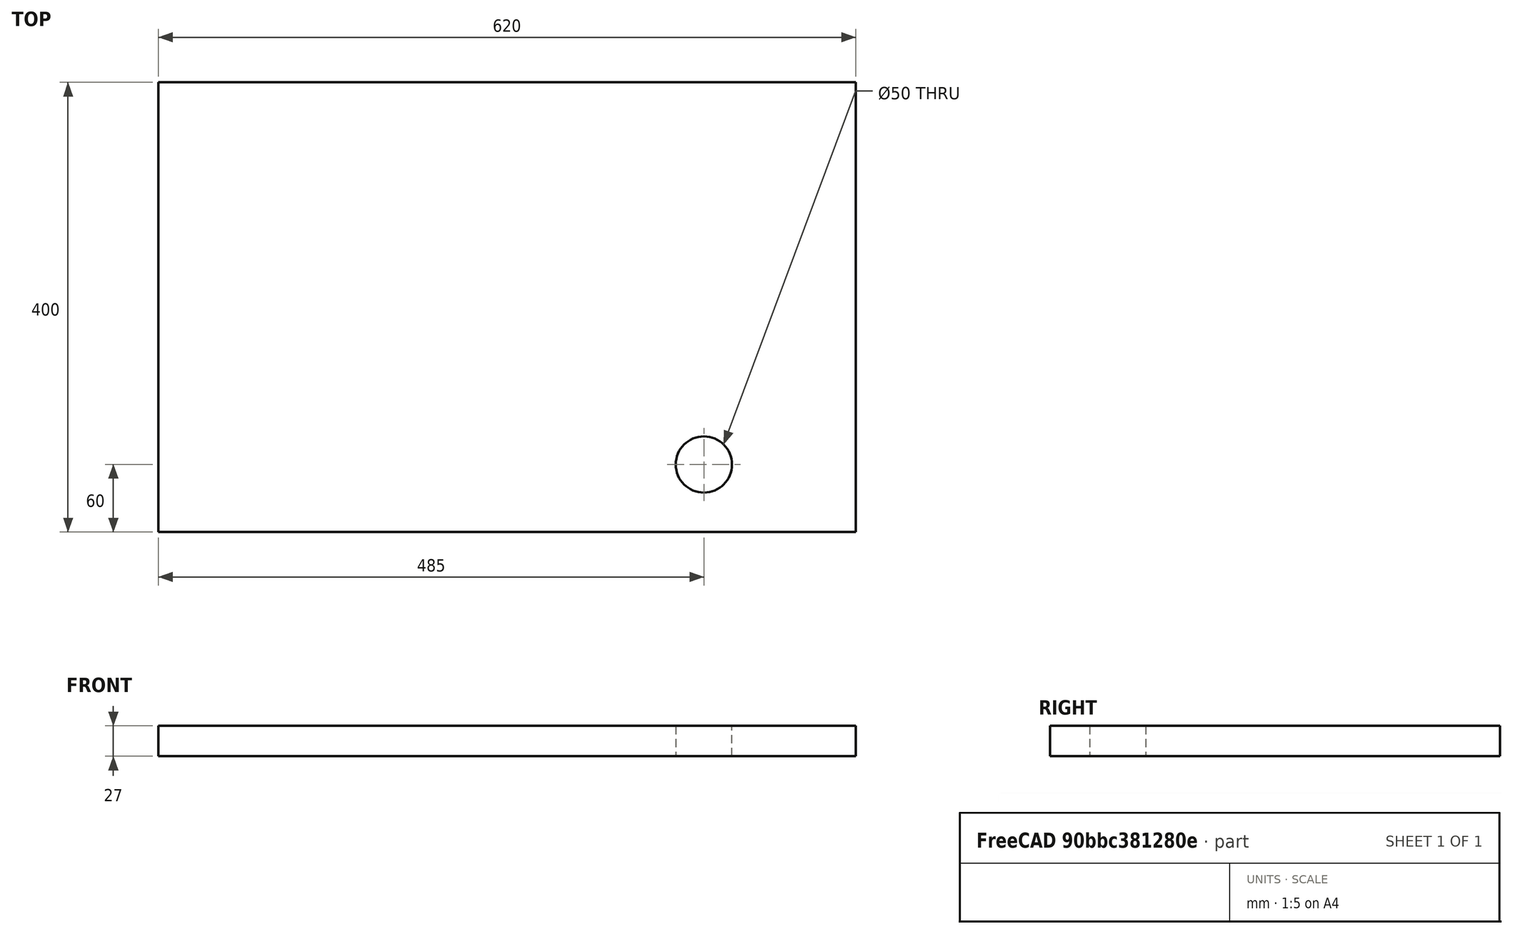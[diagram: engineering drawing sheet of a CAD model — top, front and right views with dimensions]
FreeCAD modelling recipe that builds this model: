
FCSTD DOCUMENT  (FreeCAD 0.20R25131 (Git))
Label: Arbeitsfläche
License: All rights reserved
LicenseURL: http://en.wikipedia.org/wiki/All_rights_reserved
objects: Part::FeaturePython×8, App::FeaturePython×2, Part::Box×1, Part::Cylinder×1, Part::Cut×1
note: 10 computed .brp shape members not serialized (recipe doc carries the construction recipe); baked Part::Feature solids carry a one-line shape summary decoded from their .brp
EXTERNAL_REF file=Grunddaten.FCStd obj=Spreadsheet

FEATURE [Part::Box] Box  label="Cube"
  AttacherType = Attacher::AttachEngine3D
  Height = 27
  Length = 620
  Width = 400
  expr: Length = <<Grunddaten>>#Spreadsheet.Arbeitsflaeche + 2 * <<Grunddaten>>#Spreadsheet.Ueberstand
  expr: Width = <<Grunddaten>>#Spreadsheet.Plattenbreite
  expr: Height = <<Grunddaten>>#Spreadsheet.Plattendicke
FEATURE [App::FeaturePython] Constraints  # WARN: FeaturePython — macro-defined, semantics opaque (R4)
  _Version = 1
FEATURE [Part::Cylinder] Cylinder  label="Schraubzwinge_oben"
  Angle = 360
  AttacherType = Attacher::AttachEngine3D
  FirstAngle = 0
  Height = 30
  Placement = pos=(485,60,0) rot=(0,0,1;0rad)
  Radius = 25
  SecondAngle = 0
  expr: .Placement.Base.x = Grunddaten#Spreadsheet.Arbeitsflaeche + Grunddaten#Spreadsheet.Ueberstand - 75mm
FEATURE [Part::Cut] Cut
  Base = -> Box
  Tool = -> Cylinder
FEATURE [Part::FeaturePython] Parts  # WARN: FeaturePython — macro-defined, semantics opaque (R4)
  Group = -> [Box,Cylinder,Cut]
  GroupMode = 0
FEATURE [Part::FeaturePython] Assembly  label="Arbeitsfläche"  # WARN: FeaturePython — macro-defined, semantics opaque (R4)
  AutoRelax = true
  BuildShape = 0
  Freeze = false
  Group = -> [Constraints,Elements,Parts]
  Verbose = false
  _SolverType = 1
  _Version = 1
FEATURE [App::FeaturePython] Elements  # WARN: FeaturePython — macro-defined, semantics opaque (R4)
  Group = -> [Element,Element001,Element002,Element003,Element004,Element005]
FEATURE [Part::FeaturePython] Element  label="Unten"  # link proxy (typed FeaturePython)
  Detach = false
  LinkTransform = true
  LinkedObject = -> Box [Face5]
  _Parent = -> Elements
FEATURE [Part::FeaturePython] Element001  label="Vorne"  # link proxy (typed FeaturePython)
  Detach = false
  LinkTransform = true
  LinkedObject = -> Box [Face3]
  _Parent = -> Elements
FEATURE [Part::FeaturePython] Element002  label="Hinten"  # link proxy (typed FeaturePython)
  Detach = false
  LinkTransform = true
  LinkedObject = -> Box [Face4]
  _Parent = -> Elements
FEATURE [Part::FeaturePython] Element003  label="Rechts"  # link proxy (typed FeaturePython)
  Detach = false
  LinkTransform = true
  LinkedObject = -> Box [Face2]
  _Parent = -> Elements
FEATURE [Part::FeaturePython] Element004  label="Links"  # link proxy (typed FeaturePython)
  Detach = false
  LinkTransform = true
  LinkedObject = -> Box [Face1]
  _Parent = -> Elements
FEATURE [Part::FeaturePython] Element005  label="Oben"  # link proxy (typed FeaturePython)
  Detach = false
  LinkTransform = true
  LinkedObject = -> Box [Face6]
  _Parent = -> Elements
